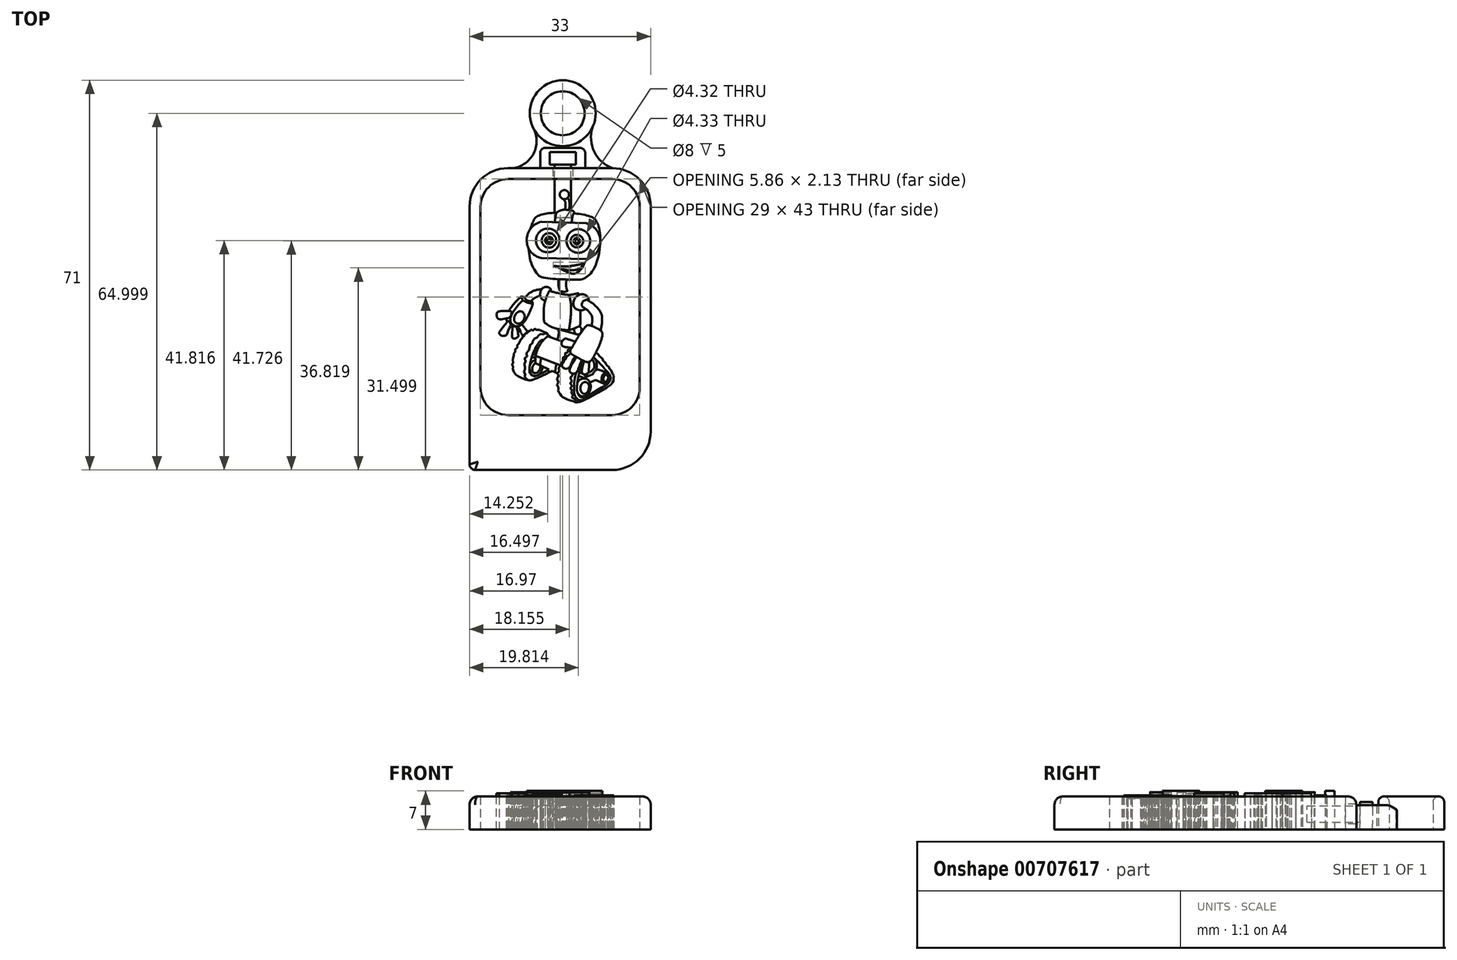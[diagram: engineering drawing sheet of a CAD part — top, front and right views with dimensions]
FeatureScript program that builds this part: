
annotation { "Feature Type Name" : "Feature", "Feature Type Description" : "" }
export const myFeature = defineFeature(function(context is Context, id is Id, definition is map)
    precondition{}
    {
        {
            var Q0;
            Q0=qCreatedBy(makeId("Top.planeOp"),FACE);
            var sketch = newSketch(context, id + "F0", { "sketchPlane" : qUnion([Q0])});
            skCircle(sketch, "E0", {"center": v(0.3, 18.7) * mm, "radius": 0.83 * mm});
            skFitSpline(sketch, "E1", {"points": [v(0.12, 17.9) * mm, v(0.47, 17.38) * mm, v(0.44, 15.96) * mm], "startDerivative": vector(0.9, -1.14) * mm, "endDerivative": vector(-0.07, -2.7) * mm});
            skFitSpline(sketch, "E2", {"points": [v(0.91, 18.15) * mm, v(1.19, 17.54) * mm, v(1.2, 15.9) * mm], "startDerivative": vector(0.78, -1.27) * mm, "endDerivative": vector(-0.02, -2.88) * mm});
            skCircle(sketch, "E3", {"center": v(-2.5, 10.36) * mm, "radius": 0.33 * mm});
            skCircle(sketch, "E4", {"center": v(-2.5, 10.36) * mm, "radius": 0.69 * mm});
            skCircle(sketch, "E5", {"center": v(-2.5, 10.36) * mm, "radius": 1.31 * mm});
            skCircle(sketch, "E6", {"center": v(2.58, 10.23) * mm, "radius": 0.33 * mm});
            skCircle(sketch, "E7", {"center": v(2.58, 10.23) * mm, "radius": 0.59 * mm});
            skCircle(sketch, "E8", {"center": v(2.58, 10.23) * mm, "radius": 1.15 * mm});
            skCircle(sketch, "E9", {"center": v(2.84, 10.27) * mm, "radius": 2.16 * mm});
            skPoint(sketch, "E9.first.point", {"position": v(4.19, 8.57) * mm});
            skPoint(sketch, "E9.second.point", {"position": v(4.6, 11.53) * mm});
            skPoint(sketch, "E9.third.point", {"position": v(0.83, 11.06) * mm});
            skCircle(sketch, "E10", {"center": v(-2.72, 10.36) * mm, "radius": 2.16 * mm});
            skPoint(sketch, "E10.first.point", {"position": v(-4.8, 10.92) * mm});
            skPoint(sketch, "E10.second.point", {"position": v(-3.27, 8.27) * mm});
            skPoint(sketch, "E10.third.point", {"position": v(-0.74, 11.23) * mm});
            skArc(sketch, "E11", {"start": v(-3.9, 13.75) * mm, "mid": v(-6.58, 10.45) * mm, "end": v(-3.92, 7.14) * mm});
            skArc(sketch, "E12", {"start": v(4.26, 6.95) * mm, "mid": v(6.85, 10.2) * mm, "end": v(4.28, 13.48) * mm});
            skLineSegment(sketch, "E13", {"start": v(-3.9, 13.75) * mm, "end": v(4.28, 13.48) * mm});
            skLineSegment(sketch, "E14", {"start": v(4.26, 6.95) * mm, "end": v(-3.92, 7.14) * mm});
            skFitSpline(sketch, "E15", {"points": [v(-1.45, 13.67) * mm, v(-1.34, 14.52) * mm, v(-1.2, 15.22) * mm, v(-1.1, 15.44) * mm, v(-0.38, 15.83) * mm, v(0.25, 15.96) * mm, v(0.44, 15.96) * mm, v(1.6, 15.83) * mm, v(2.03, 15.62) * mm, v(2.14, 15.45) * mm, v(2.16, 15.35) * mm, v(2.13, 15.29) * mm, v(2.02, 15.27) * mm, v(1.88, 15.13) * mm, v(1.62, 13.57) * mm], "startDerivative": vector(0.63, 8.93) * mm, "endDerivative": vector(-1.73, -15.25) * mm});
            skFitSpline(sketch, "E16", {"points": [v(-5.9, 12.47) * mm, v(-5.25, 14.1) * mm, v(-4.61, 14.77) * mm, v(-2.92, 15.27) * mm, v(-1.14, 15.4) * mm], "startDerivative": vector(2.4, 6.84) * mm, "endDerivative": vector(6.47, 0.13) * mm});
            skFitSpline(sketch, "E17", {"points": [v(-6.22, 8.92) * mm, v(-5.75, 6.26) * mm, v(-4.69, 4.3) * mm, v(-4.2, 3.84) * mm, v(-2.5, 3.43) * mm, v(0.92, 3.23) * mm, v(3.35, 3.25) * mm, v(4.25, 3.62) * mm, v(5.1, 4.38) * mm, v(6.1, 6.12) * mm, v(6.84, 10.02) * mm, v(6.6, 12.73) * mm, v(6.13, 13.9) * mm, v(5.7, 14.4) * mm, v(5.07, 14.7) * mm, v(3.8, 15.05) * mm, v(2.13, 15.29) * mm], "startDerivative": vector(2.92, -34.4) * mm, "endDerivative": vector(-27.68, 3.02) * mm});
            skFitSpline(sketch, "E18", {"points": [v(-1.75, 5.73) * mm, v(0.46, 5.61) * mm, v(2.53, 5.87) * mm, v(3.44, 6.09) * mm, v(4.12, 6.42) * mm], "startDerivative": vector(6.97, -0.72) * mm, "endDerivative": vector(3.62, 2.06) * mm});
            skFitSpline(sketch, "E19", {"points": [v(-1.75, 5.73) * mm, v(-0.96, 5.5) * mm, v(-0.2, 5.08) * mm, v(0.9, 4.56) * mm, v(1.74, 4.3) * mm, v(2.27, 4.34) * mm, v(3.1, 4.89) * mm, v(3.8, 5.89) * mm, v(3.9, 6.18) * mm, v(4.12, 6.42) * mm], "startDerivative": vector(7, -1.48) * mm, "endDerivative": vector(3.55, 3.32) * mm});
            skFitSpline(sketch, "E20", {"points": [v(-0.14, 5.6) * mm, v(-0.03, 5.1) * mm], "startDerivative": vector(0.1, -0.52) * mm, "endDerivative": vector(0.1, -0.52) * mm});
            skFitSpline(sketch, "E21", {"points": [v(-0.03, 5.1) * mm, v(0.8, 4.95) * mm, v(1.93, 4.94) * mm, v(2.96, 5.2) * mm, v(3.46, 5.49) * mm], "startDerivative": vector(3.26, -0.68) * mm, "endDerivative": vector(2.23, 1.53) * mm});
            skFitSpline(sketch, "E22", {"points": [v(3.46, 5.49) * mm, v(3.57, 6.14) * mm], "startDerivative": vector(0.1, 0.65) * mm, "endDerivative": vector(0.1, 0.65) * mm});
            skFitSpline(sketch, "E23", {"points": [v(-0.7, 1.73) * mm, v(-1, 1.68) * mm, v(-1.52, 1.57) * mm, v(-2.17, 1.34) * mm, v(-2.34, 1.21) * mm, v(-1.9, 1.02) * mm, v(-0.46, 0.67) * mm, v(0.7, 0.47) * mm, v(1.12, 0.44) * mm, v(1.38, 0.45) * mm, v(1.8, 0.52) * mm, v(2.6, 0.69) * mm, v(2.77, 0.77) * mm, v(2.73, 0.86) * mm, v(2.54, 1.01) * mm, v(1.61, 1.37) * mm, v(0.7, 1.58) * mm], "startDerivative": vector(-6.76, -0.7) * mm, "endDerivative": vector(-10.1, 1.55) * mm});
            skFitSpline(sketch, "E24", {"points": [v(-0.76, 3.3) * mm, v(-0.8, 2.67) * mm, v(-0.75, 1.97) * mm, v(-0.57, 1.3) * mm, v(-0.45, 1.13) * mm], "startDerivative": vector(-0.24, -2.28) * mm, "endDerivative": vector(0.93, -0.81) * mm});
            skFitSpline(sketch, "E25", {"points": [v(0.74, 3.24) * mm, v(0.64, 2.9) * mm, v(0.6, 2.27) * mm, v(0.66, 1.73) * mm, v(0.81, 1.31) * mm, v(0.85, 1.18) * mm], "startDerivative": vector(-0.63, -1.61) * mm, "endDerivative": vector(-0.1, -1.03) * mm});
            skFitSpline(sketch, "E26", {"points": [v(-0.45, 1.13) * mm, v(-0.22, 1.06) * mm, v(0.33, 1.01) * mm, v(0.7, 1.09) * mm, v(0.85, 1.18) * mm], "startDerivative": vector(0.96, -0.5) * mm, "endDerivative": vector(0.36, 0.85) * mm});
            skFitSpline(sketch, "E27", {"points": [v(1.12, 0.44) * mm, v(1.24, 0.2) * mm, v(1.38, -0.41) * mm, v(1.53, -1.74) * mm, v(1.38, -4.22) * mm, v(1.12, -5.92) * mm, v(1.04, -6) * mm, v(0.22, -5.93) * mm, v(-1.19, -5.72) * mm, v(-2.27, -5.29) * mm, v(-3.16, -4.72) * mm, v(-3.32, -4.57) * mm, v(-3.39, -4.44) * mm, v(-3.47, -3.34) * mm, v(-3.46, -2.3) * mm, v(-3.3, -1.07) * mm, v(-2.8, 0.44) * mm, v(-2.44, 1.14) * mm, v(-2.33, 1.25) * mm], "startDerivative": vector(7.24, -3.6) * mm, "endDerivative": vector(4.32, 3.3) * mm});
            skFitSpline(sketch, "E28", {"points": [v(1.04, -6) * mm, v(1.39, -5.9) * mm, v(2.36, -5.56) * mm, v(2.9, -5.32) * mm, v(3.1, -5.2) * mm, v(3.18, -5) * mm, v(3.21, -4.58) * mm, v(3.19, -2.37) * mm], "startDerivative": vector(2.66, 0.6) * mm, "endDerivative": vector(-0.15, 9.68) * mm});
            skFitSpline(sketch, "E29", {"points": [v(2.77, 0.79) * mm, v(2.82, 0.7) * mm, v(2.87, 0.37) * mm], "startDerivative": vector(0.07, -0.11) * mm, "endDerivative": vector(0.06, -0.59) * mm});
            skFitSpline(sketch, "E30", {"points": [v(-3.17, -0.58) * mm, v(-3.39, -0.55) * mm, v(-3.82, -0.28) * mm, v(-4.1, 0.29) * mm, v(-4.04, 1.06) * mm, v(-3.73, 1.58) * mm, v(-3.27, 1.86) * mm, v(-2.76, 1.88) * mm, v(-2.36, 1.68) * mm, v(-2.22, 1.54) * mm, v(-2.11, 1.36) * mm], "startDerivative": vector(-2.86, 0.03) * mm, "endDerivative": vector(1.55, -2.75) * mm});
            skFitSpline(sketch, "E31", {"points": [v(4.2, -2.1) * mm, v(3.83, -2.28) * mm, v(3.38, -2.4) * mm, v(3.19, -2.37) * mm, v(2.56, -2.2) * mm, v(2.14, -1.83) * mm, v(1.93, -1.09) * mm, v(2.2, -0.2) * mm, v(2.56, 0.19) * mm, v(2.87, 0.37) * mm, v(3.37, 0.54) * mm, v(4, 0.47) * mm, v(4.49, 0.12) * mm, v(4.73, -0.35) * mm, v(4.76, -0.66) * mm], "startDerivative": vector(-4.5, -3.3) * mm, "endDerivative": vector(0.01, -5.32) * mm});
            skFitSpline(sketch, "E32", {"points": [v(-3.48, -3.22) * mm, v(-1.78, -4.06) * mm, v(1.36, -4.43) * mm, v(3.2, -3.79) * mm], "startDerivative": vector(4.9, -3.02) * mm, "endDerivative": vector(5.37, 2.7) * mm});
            skFitSpline(sketch, "E33", {"points": [v(-3.84, 1.46) * mm, v(-4.94, 1.3) * mm, v(-6.15, 0.68) * mm, v(-6.87, -0.09) * mm], "startDerivative": vector(-3.3, -0.27) * mm, "endDerivative": vector(-2.02, -2.53) * mm});
            skFitSpline(sketch, "E34", {"points": [v(-4.08, 0.2) * mm, v(-4.4, 0.17) * mm, v(-5.23, -0.2) * mm, v(-5.69, -0.66) * mm], "startDerivative": vector(-1.12, 0.03) * mm, "endDerivative": vector(-1.09, -1.4) * mm});
            skFitSpline(sketch, "E35", {"points": [v(-6.87, -0.09) * mm, v(-6.78, -0.35) * mm, v(-6.22, -0.66) * mm, v(-5.8, -0.72) * mm, v(-5.69, -0.66) * mm], "startDerivative": vector(0.17, -1.2) * mm, "endDerivative": vector(0.62, 0.48) * mm});
            skFitSpline(sketch, "E36", {"points": [v(-5.65, -0.61) * mm, v(-5.52, -0.96) * mm, v(-5.55, -1.08) * mm, v(-5.79, -1.1) * mm, v(-6.43, -0.95) * mm, v(-7.26, -0.55) * mm, v(-7.32, -0.47) * mm, v(-7.53, 0.04) * mm, v(-7.46, 0.1) * mm, v(-6.84, -0.04) * mm], "startDerivative": vector(1.46, -3.36) * mm, "endDerivative": vector(5.12, -1.6) * mm});
            skFitSpline(sketch, "E37", {"points": [v(-7.4, 0.1) * mm, v(-7.53, 0.13) * mm, v(-7.7, 0.04) * mm, v(-8.25, -0.5) * mm, v(-9.37, -1.76) * mm, v(-9.7, -2.26) * mm, v(-9.85, -2.52) * mm], "startDerivative": vector(-1.54, 0.55) * mm, "endDerivative": vector(-1.06, -1.93) * mm});
            skFitSpline(sketch, "E38", {"points": [v(-5.54, -0.9) * mm, v(-5.48, -1.03) * mm, v(-5.48, -1.23) * mm, v(-6.29, -3.27) * mm, v(-6.98, -4.42) * mm, v(-7.46, -4.94) * mm, v(-8, -5.24) * mm, v(-8.74, -5.2) * mm, v(-9.4, -4.73) * mm, v(-9.52, -3.77) * mm, v(-9.1, -2.76) * mm, v(-8.38, -1.75) * mm, v(-7.3, -0.5) * mm], "startDerivative": vector(2.07, -4.05) * mm, "endDerivative": vector(10.06, 11.15) * mm});
            skEllipse(sketch, "E39", {"center": v(-7.91, -3.7) * mm, "majorRadius": 1.17 * mm, "minorRadius": 0.9 * mm, "majorAxis": v(0.45, 0.9)});
            skFitSpline(sketch, "E40", {"points": [v(-9.85, -3.75) * mm, v(-11.14, -4) * mm, v(-11.6, -4) * mm, v(-11.94, -3.67) * mm, v(-12.06, -3) * mm, v(-11.93, -2.73) * mm, v(-11.68, -2.58) * mm, v(-11.07, -2.52) * mm, v(-9.85, -2.52) * mm], "startDerivative": vector(-8, -1.73) * mm, "endDerivative": vector(7.43, -0.04) * mm});
            skFitSpline(sketch, "E41", {"points": [v(-9.85, -3.75) * mm, v(-9.6, -3.57) * mm, v(-9.39, -3.2) * mm, v(-9.34, -2.7) * mm, v(-9.52, -2.52) * mm, v(-9.85, -2.52) * mm], "startDerivative": vector(1.43, 0.8) * mm, "endDerivative": vector(-1.85, -0.22) * mm});
            skFitSpline(sketch, "E42", {"points": [v(4.38, -0.46) * mm, v(4.76, -0.66) * mm, v(5.4, -1.08) * mm, v(6.04, -1.64) * mm, v(6.54, -2.18) * mm, v(7.06, -3.11) * mm, v(7.16, -4.62) * mm, v(6.9, -6.06) * mm], "startDerivative": vector(3.69, -1.9) * mm, "endDerivative": vector(-2.34, -7.83) * mm});
            skFitSpline(sketch, "E43", {"points": [v(3.66, -1.78) * mm, v(4.2, -2.1) * mm, v(4.87, -2.73) * mm, v(5.32, -3.49) * mm, v(5.34, -4.62) * mm, v(5.24, -5.2) * mm], "startDerivative": vector(2.71, -1.62) * mm, "endDerivative": vector(-1.18, -2.93) * mm});
            skFitSpline(sketch, "E44", {"points": [v(6.9, -6.06) * mm, v(7.16, -6.34) * mm, v(7.23, -6.83) * mm, v(6.74, -8.54) * mm, v(5.58, -10.93) * mm, v(5.1, -11.56) * mm, v(4.63, -11.8) * mm, v(3.71, -11.54) * mm, v(1.8, -10.47) * mm, v(1.45, -10.2) * mm, v(1.37, -9.71) * mm, v(1.59, -9.3) * mm, v(2.54, -7.66) * mm, v(3.61, -6.06) * mm, v(4.2, -5.3) * mm, v(4.43, -5.1) * mm, v(5.24, -5.2) * mm, v(6.9, -6.06) * mm]});
            skFitSpline(sketch, "E45", {"points": [v(2.3, -8.07) * mm, v(0.6, -7.54) * mm, v(0.42, -7.54) * mm, v(0, -7.87) * mm, v(-0.23, -8.54) * mm, v(-0.05, -8.88) * mm, v(0.5, -9.08) * mm, v(1.68, -9.17) * mm], "startDerivative": vector(-9.45, 3.1) * mm, "endDerivative": vector(6.78, -0.26) * mm});
            skFitSpline(sketch, "E46", {"points": [v(3.87, -11.61) * mm, v(3.62, -12.64) * mm, v(3.48, -13.45) * mm, v(3.59, -13.84) * mm, v(3.9, -14.03) * mm, v(4.39, -13.95) * mm, v(4.76, -13.6) * mm, v(4.76, -13.41) * mm, v(4.85, -11.74) * mm], "startDerivative": vector(-1.62, -6.5) * mm, "endDerivative": vector(0.7, 10.55) * mm});
            skFitSpline(sketch, "E47", {"points": [v(3.5, -11.43) * mm, v(2.64, -13.52) * mm, v(2.48, -13.76) * mm, v(1.9, -13.9) * mm, v(1.36, -13.66) * mm, v(1.26, -13.3) * mm, v(1.44, -12.67) * mm, v(2.53, -10.9) * mm], "startDerivative": vector(-4.72, -11.44) * mm, "endDerivative": vector(5.93, 9.05) * mm});
            skFitSpline(sketch, "E48", {"points": [v(2.27, -10.74) * mm, v(1.68, -11.81) * mm, v(1.26, -12.74) * mm, v(0.92, -12.97) * mm, v(0.34, -12.97) * mm, v(-0.14, -12.43) * mm, v(0.2, -11.65) * mm, v(0.86, -10.73) * mm, v(1.45, -10.2) * mm], "startDerivative": vector(-3.77, -6.76) * mm, "endDerivative": vector(4.2, 4.03) * mm});
            skFitSpline(sketch, "E49", {"points": [v(3.66, -1.78) * mm, v(3.48, -1.45) * mm, v(3.71, -0.73) * mm, v(4.38, -0.46) * mm], "startDerivative": vector(-0.94, 1.03) * mm, "endDerivative": vector(1.87, 0.43) * mm});
            skFitSpline(sketch, "E50", {"points": [v(1.6, -9.27) * mm, v(1.43, -9.26) * mm, v(1.38, -9.44) * mm, v(0.97, -9.54) * mm, v(0.86, -10.03) * mm, v(0.46, -10.2) * mm, v(0.48, -10.7) * mm, v(0.05, -10.97) * mm, v(0.07, -11.56) * mm, v(-0.23, -11.9) * mm, v(-0.38, -12.43) * mm, v(-0.7, -12.82) * mm, v(-0.7, -13.5) * mm, v(-0.98, -13.83) * mm, v(-0.79, -14.3) * mm, v(-1.05, -14.84) * mm, v(-0.8, -15.5) * mm, v(-1.05, -15.84) * mm, v(-0.76, -16.5) * mm, v(-0.84, -16.9) * mm, v(-0.46, -17.65) * mm, v(0.2, -18.28) * mm, v(2.04, -19.01) * mm, v(3.13, -19.05) * mm, v(8.56, -16.08) * mm, v(9.01, -15.65) * mm, v(9.15, -15.34) * mm, v(9.27, -15.14) * mm, v(9.21, -14.97) * mm, v(9.34, -14.75) * mm, v(9.22, -14.49) * mm, v(9.3, -14.28) * mm, v(9.09, -13.91) * mm, v(9.1, -13.77) * mm, v(8.78, -13.4) * mm, v(8.8, -13.21) * mm, v(8.42, -12.89) * mm, v(8.5, -12.75) * mm, v(8.04, -12.43) * mm, v(8.07, -12.32) * mm, v(7.7, -11.97) * mm, v(7.73, -11.8) * mm, v(7.36, -11.56) * mm, v(7.37, -11.31) * mm, v(7, -11.1) * mm, v(7.02, -10.98) * mm, v(6.72, -10.73) * mm, v(6.7, -10.61) * mm, v(6.38, -10.44) * mm, v(6.38, -10.26) * mm, v(6.04, -10.08) * mm], "startDerivative": vector(-15.2, 2.24) * mm, "endDerivative": vector(-28.52, 9.44) * mm});
            skFitSpline(sketch, "E51", {"points": [v(1.67, -13.87) * mm, v(1.76, -14.28) * mm, v(1.38, -14.65) * mm, v(1.68, -15.3) * mm, v(1.38, -15.62) * mm, v(1.68, -16.15) * mm, v(1.38, -16.5) * mm, v(1.68, -16.92) * mm, v(1.59, -17.5) * mm, v(1.87, -17.85) * mm, v(1.68, -18.2) * mm, v(2.3, -18.66) * mm, v(2.48, -18.94) * mm, v(3.13, -19.05) * mm], "startDerivative": vector(3.43, -6.3) * mm, "endDerivative": vector(10.14, -0.04) * mm});
            skFitSpline(sketch, "E52", {"points": [v(2.48, -13.76) * mm, v(2.24, -14.48) * mm, v(2.06, -16.55) * mm, v(2.2, -17.86) * mm, v(2.9, -18.7) * mm, v(3.92, -18.64) * mm, v(4.67, -18.36) * mm], "startDerivative": vector(-1.23, -4.5) * mm, "endDerivative": vector(4.87, 2.34) * mm});
            skFitSpline(sketch, "E53", {"points": [v(3.71, -11.54) * mm, v(3.17, -13.15) * mm, v(2.74, -15.07) * mm, v(2.68, -17.36) * mm, v(3.27, -18.17) * mm, v(4.2, -18.1) * mm, v(7.11, -16.42) * mm, v(8.4, -15.53) * mm, v(8.72, -14.56) * mm, v(8.07, -13.52) * mm, v(6.64, -11.91) * mm, v(5.58, -10.93) * mm], "startDerivative": vector(-6.92, -17.06) * mm, "endDerivative": vector(-12.58, 10.17) * mm});
            skFitSpline(sketch, "E54", {"points": [v(2.65, -15.66) * mm, v(3.13, -15.01) * mm, v(4.2, -14.82) * mm, v(4.87, -15.37) * mm, v(5.1, -16.33) * mm, v(4.73, -17.48) * mm, v(4.2, -17.94) * mm, v(3.71, -18.07) * mm, v(3.13, -17.92) * mm, v(2.68, -17.36) * mm], "startDerivative": vector(3.07, 6.78) * mm, "endDerivative": vector(-2.95, 6.13) * mm});
            skLineSegment(sketch, "E55", {"start": v(4.2, -14.82) * mm, "end": v(2.88, -14.32) * mm});
            skLineSegment(sketch, "E56", {"start": v(4.95, -15.52) * mm, "end": v(5.98, -15.08) * mm});
            skLineSegment(sketch, "E57", {"start": v(5.98, -15.08) * mm, "end": v(7.58, -15.75) * mm});
            skEllipse(sketch, "E58", {"center": v(4.01, -16.5) * mm, "majorRadius": 1.09 * mm, "minorRadius": 0.78 * mm, "majorAxis": v(0.16, 0.99)});
            skEllipse(sketch, "E59", {"center": v(7.83, -14.75) * mm, "majorRadius": 0.63 * mm, "minorRadius": 0.45 * mm, "majorAxis": v(0.27, 0.96)});
            skEllipse(sketch, "E60", {"center": v(7.83, -14.75) * mm, "majorRadius": 1.03 * mm, "minorRadius": 0.75 * mm, "majorAxis": v(-0.24, -0.97)});
            skFitSpline(sketch, "E61", {"points": [v(5.98, -15.08) * mm, v(5.62, -14.73) * mm, v(5.5, -14.2) * mm, v(5.65, -13.69) * mm, v(5.98, -13.32) * mm, v(6.33, -13.16) * mm, v(6.48, -13.17) * mm], "startDerivative": vector(-2.22, 1.68) * mm, "endDerivative": vector(1.4, -0.29) * mm});
            skLineSegment(sketch, "E62", {"start": v(6.48, -13.17) * mm, "end": v(8.14, -13.77) * mm});
            skLineSegment(sketch, "E63", {"start": v(3.79, -14.66) * mm, "end": v(5.52, -14) * mm});
            skFitSpline(sketch, "E64", {"points": [v(3.04, -13.64) * mm, v(4.2, -14.23) * mm, v(4.52, -14.3) * mm, v(4.9, -14.24) * mm], "startDerivative": vector(2.74, -1.49) * mm, "endDerivative": vector(1.52, 0.33) * mm});
            skFitSpline(sketch, "E65", {"points": [v(5.8, -11.1) * mm, v(6.2, -11.92) * mm, v(6.11, -13.04) * mm, v(5.98, -13.32) * mm], "startDerivative": vector(1.4, -1.95) * mm, "endDerivative": vector(-0.64, -1) * mm});
            skFitSpline(sketch, "E66", {"points": [v(3.43, -12.3) * mm, v(3.4, -12.94) * mm, v(3.48, -13.45) * mm], "startDerivative": vector(-0.12, -1.25) * mm, "endDerivative": vector(0.22, -1.05) * mm});
            skFitSpline(sketch, "E67", {"points": [v(5.26, -11.4) * mm, v(5.57, -11.6) * mm, v(5.77, -12.6) * mm, v(5.38, -13.32) * mm, v(4.94, -13.63) * mm, v(4.73, -13.65) * mm], "startDerivative": vector(1.96, -0.71) * mm, "endDerivative": vector(-1.59, 0.06) * mm});
            skLineSegment(sketch, "E68", {"start": v(-2.77, -7.1) * mm, "end": v(-0.11, -8.05) * mm});
            skFitSpline(sketch, "E69", {"points": [v(-2.77, -7.1) * mm, v(-3.76, -8.1) * mm, v(-4.58, -9.48) * mm, v(-4.98, -11) * mm, v(-4.98, -12.02) * mm], "startDerivative": vector(-4.13, -3.72) * mm, "endDerivative": vector(0.28, -4.5) * mm});
            skLineSegment(sketch, "E70", {"start": v(-4.98, -12.02) * mm, "end": v(-0.98, -13.83) * mm});
            skLineSegment(sketch, "E71", {"start": v(-4.94, -10.69) * mm, "end": v(-0.38, -12.43) * mm});
            skFitSpline(sketch, "E72", {"points": [v(-3.9, -11.08) * mm, v(-4.04, -11.64) * mm, v(-4.07, -12.43) * mm], "startDerivative": vector(-0.58, -1.59) * mm, "endDerivative": vector(0.13, -1.26) * mm});
            skFitSpline(sketch, "E73", {"points": [v(-1.11, -12.15) * mm, v(-1.3, -12.88) * mm, v(-1.33, -13.68) * mm], "startDerivative": vector(-0.59, -1.61) * mm, "endDerivative": vector(0.18, -1.44) * mm});
            skFitSpline(sketch, "E74", {"points": [v(-10.25, -3.83) * mm, v(-10.23, -4.14) * mm, v(-10.1, -4.43) * mm], "startDerivative": vector(0, -0.64) * mm, "endDerivative": vector(0.32, -0.56) * mm});
            skFitSpline(sketch, "E75", {"points": [v(-10.1, -4.43) * mm, v(-11.55, -6.34) * mm, v(-11.6, -6.47) * mm, v(-11.5, -6.69) * mm, v(-11.18, -6.98) * mm, v(-10.8, -7.04) * mm, v(-10.32, -6.92) * mm, v(-10.21, -6.75) * mm, v(-9.48, -5.02) * mm, v(-9.5, -4.87) * mm, v(-9.71, -4.49) * mm, v(-9.84, -4.37) * mm, v(-10.04, -4.37) * mm, v(-10.1, -4.43) * mm]});
            skFitSpline(sketch, "E76", {"points": [v(-9.48, -5.02) * mm, v(-9, -5.24) * mm, v(-8.42, -5.34) * mm, v(-8, -5.24) * mm], "startDerivative": vector(1.34, -0.74) * mm, "endDerivative": vector(1.3, 0.44) * mm});
            skFitSpline(sketch, "E77", {"points": [v(-9.15, -5.18) * mm, v(-9.24, -7.14) * mm, v(-9.2, -7.4) * mm, v(-8.88, -7.52) * mm, v(-8.59, -7.46) * mm, v(-8.19, -7.2) * mm, v(-8.09, -6.96) * mm, v(-8.42, -5.34) * mm], "startDerivative": vector(-0.42, -9.45) * mm, "endDerivative": vector(-2.16, 8.56) * mm});
            skFitSpline(sketch, "E78", {"points": [v(-2.33, -7.25) * mm, v(-2.32, -7.1) * mm, v(-2.67, -6.94) * mm, v(-2.67, -6.77) * mm, v(-4.55, -5.92) * mm, v(-4.84, -5.92) * mm, v(-5.1, -5.76) * mm, v(-5.47, -6.03) * mm, v(-5.8, -5.9) * mm, v(-6.01, -6.18) * mm, v(-6.3, -6.17) * mm, v(-6.48, -6.55) * mm, v(-6.88, -6.62) * mm, v(-7, -7.05) * mm, v(-7.35, -7.14) * mm, v(-7.42, -7.6) * mm, v(-7.8, -7.83) * mm, v(-7.86, -8.37) * mm, v(-8.27, -8.66) * mm, v(-8.27, -9.1) * mm, v(-8.65, -9.47) * mm, v(-8.68, -10.02) * mm, v(-8.97, -10.35) * mm, v(-8.87, -10.76) * mm, v(-9.15, -11.23) * mm, v(-9, -11.77) * mm, v(-9.21, -12.18) * mm, v(-9.02, -12.66) * mm, v(-9.1, -13.05) * mm, v(-8.66, -14) * mm, v(-8.24, -14.36) * mm, v(-6.87, -14.98) * mm, v(-5.82, -15.11) * mm, v(-1.92, -13.4) * mm], "startDerivative": vector(4.57, 10.26) * mm, "endDerivative": vector(54.83, 27.76) * mm});
            skFitSpline(sketch, "E79", {"points": [v(-8.12, -5.28) * mm, v(-7.37, -6.88) * mm, v(-7.23, -6.96) * mm, v(-6.96, -6.94) * mm], "startDerivative": vector(1.52, -3.53) * mm, "endDerivative": vector(1.33, 0.21) * mm});
            skFitSpline(sketch, "E80", {"points": [v(-7.46, -4.94) * mm, v(-7.05, -5.44) * mm, v(-6.6, -6.02) * mm, v(-6.53, -6.13) * mm, v(-6.52, -6.4) * mm, v(-6.6, -6.58) * mm], "startDerivative": vector(1.44, -1.7) * mm, "endDerivative": vector(-0.68, -1.04) * mm});
            skFitSpline(sketch, "E81", {"points": [v(-2.67, -6.77) * mm, v(-3.04, -6.63) * mm, v(-3.34, -6.55) * mm, v(-3.72, -6.77) * mm, v(-4, -6.66) * mm, v(-4.22, -6.96) * mm, v(-4.5, -6.96) * mm, v(-4.66, -7.33) * mm, v(-5.04, -7.4) * mm, v(-5.13, -7.8) * mm, v(-5.49, -7.92) * mm, v(-5.56, -8.4) * mm, v(-5.9, -8.54) * mm, v(-5.94, -9.12) * mm, v(-6.26, -9.37) * mm, v(-6.2, -9.85) * mm, v(-6.7, -10.26) * mm, v(-6.48, -10.86) * mm, v(-6.93, -11.14) * mm, v(-6.74, -11.68) * mm, v(-7.05, -12.02) * mm, v(-6.75, -12.47) * mm, v(-7.07, -12.82) * mm, v(-6.84, -13.2) * mm, v(-7.05, -13.67) * mm, v(-6.78, -14.01) * mm, v(-7.06, -14.29) * mm, v(-6.65, -14.67) * mm, v(-6.61, -14.96) * mm, v(-6.17, -15.15) * mm], "startDerivative": vector(-11.53, 3.84) * mm, "endDerivative": vector(16.6, -3.55) * mm});
            skFitSpline(sketch, "E82", {"points": [v(-2.48, -13.16) * mm, v(-4.42, -14.13) * mm, v(-5.25, -14.35) * mm, v(-5.96, -13.83) * mm, v(-5.98, -12.31) * mm, v(-5.38, -10.14) * mm, v(-4.22, -8.1) * mm, v(-3.76, -7.79) * mm, v(-3.5, -7.79) * mm], "startDerivative": vector(-12.89, -6.58) * mm, "endDerivative": vector(4.5, -0.52) * mm});
            skFitSpline(sketch, "E83", {"points": [v(-3.72, -12.6) * mm, v(-3.72, -12.97) * mm, v(-3.98, -13.62) * mm, v(-4.65, -14.24) * mm, v(-5.24, -14.3) * mm, v(-5.74, -14.02) * mm, v(-5.97, -13.44) * mm, v(-6.03, -12.64) * mm, v(-5.67, -11.88) * mm, v(-5.2, -11.5) * mm, v(-5, -11.43) * mm], "startDerivative": vector(0.38, -4.4) * mm, "endDerivative": vector(2.97, 0.62) * mm});
            skFitSpline(sketch, "E84", {"points": [v(-5.65, -10.9) * mm, v(-5.2, -11) * mm, v(-5, -11.19) * mm], "startDerivative": vector(0.57, -0.15) * mm, "endDerivative": vector(0.38, -0.44) * mm});
            skFitSpline(sketch, "E85", {"points": [v(-5.43, -10.26) * mm, v(-4.91, -10.55) * mm], "startDerivative": vector(0.52, -0.28) * mm, "endDerivative": vector(0.52, -0.28) * mm});
            skFitSpline(sketch, "E86", {"points": [v(-4.73, -8.82) * mm, v(-4.98, -9.84) * mm, v(-4.87, -10.35) * mm], "startDerivative": vector(-1.14, -2.41) * mm, "endDerivative": vector(0.44, -1.13) * mm});
            skFitSpline(sketch, "E87", {"points": [v(-0.82, -5.8) * mm, v(-0.85, -5.94) * mm, v(-0.7, -6.17) * mm, v(-0.77, -6.3) * mm, v(-0.68, -6.54) * mm, v(-0.77, -6.63) * mm, v(-0.67, -6.8) * mm, v(-0.8, -6.87) * mm, v(-0.7, -7.08) * mm, v(-0.84, -7.18) * mm, v(-0.81, -7.39) * mm, v(-0.97, -7.48) * mm, v(-1, -7.63) * mm, v(-1.2, -7.66) * mm], "startDerivative": vector(-1.06, -2.03) * mm, "endDerivative": vector(-3.33, 0.28) * mm});
            skFitSpline(sketch, "E88", {"points": [v(2.17, -5.64) * mm, v(2.1, -5.99) * mm, v(2.29, -6.55) * mm, v(2.76, -6.78) * mm, v(3.22, -6.6) * mm], "startDerivative": vector(-0.53, -1.47) * mm, "endDerivative": vector(1.55, 1.3) * mm});
            skFitSpline(sketch, "E89", {"points": [v(2.98, -5.29) * mm, v(3.3, -5.53) * mm, v(3.42, -5.95) * mm, v(3.3, -6.49) * mm], "startDerivative": vector(1.17, -0.65) * mm, "endDerivative": vector(-0.68, -1.55) * mm});
            skLineSegment(sketch, "E90", {"start": v(-0.82, -5.8) * mm, "end": v(2.58, -6.75) * mm});
            skFitSpline(sketch, "E91", {"points": [v(-4.99, -11.96) * mm, v(-5.32, -12.33) * mm, v(-5.56, -13.07) * mm, v(-5.48, -13.55) * mm, v(-5.21, -13.8) * mm, v(-4.76, -13.77) * mm, v(-4.3, -13.35) * mm, v(-4.1, -12.9) * mm, v(-4.1, -12.57) * mm, v(-4.12, -12.4) * mm], "startDerivative": vector(-3.02, -2.7) * mm, "endDerivative": vector(-0.42, 2.2) * mm});
            skSolve(sketch);
        }
        {
            var Q0;
            {var subQ1=sQuery(id+"F0.wireOp",EDGE,"E44");var subQ12=makeQuery(id+"F0.imprint","INTERSECT",VERTEX,{"derivedFrom":[sQuery(id+"F0.wireOp",EDGE,"E42"),subQ1]});Q0=makeQuery(id+"F0.imprint","IMPRINT",FACE,{"disambiguationData":[TD([[makeQuery(id+"F0.imprint","IMPRINT",EDGE,{"disambiguationData":[TD([[subQ12,-1.0]])],"derivedFrom":subQ1}),-1.0]])]});}
            var Q1;
            Q1=makeQuery(id+"F0.imprint","IMPRINT",FACE,{"disambiguationData":[TD([[makeQuery(id+"F0.imprint","IMPRINT",EDGE,{"derivedFrom":sQuery(id+"F0.wireOp",EDGE,"E9")}),-1.0]])]});
            var Q2;
            {var subQ0=sQuery(id+"F0.wireOp",EDGE,"E0");var subQ1=makeQuery(id+"F0.imprint","INTERSECT",VERTEX,{"derivedFrom":[subQ0,sQuery(id+"F0.wireOp",EDGE,"E1")]});Q2=makeQuery(id+"F0.imprint","IMPRINT",FACE,{"disambiguationData":[TD([[makeQuery(id+"F0.imprint","IMPRINT",EDGE,{"disambiguationData":[TD([[subQ1,-1.0]])],"derivedFrom":subQ0}),1.0]])]});}
            extrude(context, id + "F1", {"entities" : qUnion([Q0, Q1, Q2]), "depth" : 7 * mm, "offsetDistance" : 25 * mm});
        }
        {
            var Q0;
            {var subQ0=sQuery(id+"F0.wireOp",EDGE,"E45");var subQ1=sQuery(id+"F0.wireOp",EDGE,"E44");var subQ2=makeQuery(id+"F0.imprint","INTERSECT",VERTEX,{"disambiguationData":[OD(0.0)],"derivedFrom":[subQ1,subQ0]});Q0=makeQuery(id+"F0.imprint","IMPRINT",FACE,{"disambiguationData":[TD([[makeQuery(id+"F0.imprint","IMPRINT",EDGE,{"disambiguationData":[TD([[subQ2,1.0]])],"derivedFrom":subQ1}),1.0]])]});}
            var Q1;
            {var subQ0=sQuery(id+"F0.wireOp",EDGE,"E48");Q1=makeQuery(id+"F0.imprint","IMPRINT",FACE,{"disambiguationData":[TD([[makeQuery(id+"F0.imprint","IMPRINT",EDGE,{"derivedFrom":subQ0}),-1.0]])]});}
            var Q2;
            {var subQ0=sQuery(id+"F0.wireOp",EDGE,"E47");var subQ1=sQuery(id+"F0.wireOp",EDGE,"E44");var subQ2=makeQuery(id+"F0.imprint","INTERSECT",VERTEX,{"disambiguationData":[OD(0.0)],"derivedFrom":[subQ1,subQ0]});Q2=makeQuery(id+"F0.imprint","IMPRINT",FACE,{"disambiguationData":[TD([[makeQuery(id+"F0.imprint","IMPRINT",EDGE,{"disambiguationData":[TD([[subQ2,-1.0]])],"derivedFrom":subQ1}),1.0]])]});}
            var Q3;
            {var subQ0=sQuery(id+"F0.wireOp",EDGE,"E46");var subQ1=sQuery(id+"F0.wireOp",EDGE,"E44");var subQ2=makeQuery(id+"F0.imprint","INTERSECT",VERTEX,{"disambiguationData":[OD(0.0)],"derivedFrom":[subQ1,subQ0]});Q3=makeQuery(id+"F0.imprint","IMPRINT",FACE,{"disambiguationData":[TD([[makeQuery(id+"F0.imprint","IMPRINT",EDGE,{"disambiguationData":[TD([[subQ2,1.0]])],"derivedFrom":subQ1}),1.0]])]});}
            var Q4;
            {var subQ3=sQuery(id+"F0.wireOp",EDGE,"E49");Q4=makeQuery(id+"F0.imprint","IMPRINT",FACE,{"disambiguationData":[TD([[makeQuery(id+"F0.imprint","IMPRINT",EDGE,{"derivedFrom":subQ3}),1.0]])]});}
            var Q5;
            {var subQ3=sQuery(id+"F0.wireOp",EDGE,"E27");var subQ5=sQuery(id+"F0.wireOp",EDGE,"E23");var subQ6=makeQuery(id+"F0.imprint","INTERSECT",VERTEX,{"disambiguationData":[OD(1.0)],"derivedFrom":[subQ5,subQ3]});Q5=makeQuery(id+"F0.imprint","IMPRINT",FACE,{"disambiguationData":[TD([[makeQuery(id+"F0.imprint","IMPRINT",EDGE,{"disambiguationData":[TD([[subQ6,1.0]])],"derivedFrom":subQ5}),-1.0]])]});}
            var Q6;
            Q6=makeQuery(id+"F0.imprint","IMPRINT",FACE,{"disambiguationData":[TD([[makeQuery(id+"F0.imprint","IMPRINT",EDGE,{"derivedFrom":sQuery(id+"F0.wireOp",EDGE,"E39")}),-1.0]])]});
            var Q7;
            Q7=makeQuery(id+"F0.imprint","IMPRINT",FACE,{"disambiguationData":[TD([[makeQuery(id+"F0.imprint","IMPRINT",EDGE,{"derivedFrom":sQuery(id+"F0.wireOp",EDGE,"E3")}),1.0]])]});
            var Q8;
            Q8=makeQuery(id+"F0.imprint","IMPRINT",FACE,{"disambiguationData":[TD([[makeQuery(id+"F0.imprint","IMPRINT",EDGE,{"derivedFrom":sQuery(id+"F0.wireOp",EDGE,"E6")}),1.0]])]});
            var Q9;
            {var subQ0=sQuery(id+"F0.wireOp",EDGE,"E15");var subQ3=sQuery(id+"F0.wireOp",EDGE,"E13");var subQ4=makeQuery(id+"F0.imprint","INTERSECT",VERTEX,{"disambiguationData":[OD(0.0)],"derivedFrom":[subQ3,subQ0]});Q9=makeQuery(id+"F0.imprint","IMPRINT",FACE,{"disambiguationData":[TD([[makeQuery(id+"F0.imprint","IMPRINT",EDGE,{"disambiguationData":[TD([[subQ4,-1.0]])],"derivedFrom":subQ3}),1.0]])]});}
            extrude(context, id + "F2", {"entities" : qUnion([Q0, Q1, Q2, Q3, Q4, Q5, Q6, Q7, Q8, Q9]), "depth" : 6.8 * mm, "offsetDistance" : 25 * mm});
        }
        {
            var Q0;
            {var subQ4=sQuery(id+"F0.wireOp",EDGE,"E14");Q0=makeQuery(id+"F0.imprint","IMPRINT",FACE,{"disambiguationData":[TD([[makeQuery(id+"F0.imprint","IMPRINT",EDGE,{"derivedFrom":subQ4}),1.0]])]});}
            var Q1;
            {var subQ3=sQuery(id+"F0.wireOp",EDGE,"E16");Q1=makeQuery(id+"F0.imprint","IMPRINT",FACE,{"disambiguationData":[TD([[makeQuery(id+"F0.imprint","IMPRINT",EDGE,{"derivedFrom":subQ3}),-1.0]])]});}
            var Q2;
            {var subQ0=sQuery(id+"F0.wireOp",EDGE,"E13");var subQ1=sQuery(id+"F0.wireOp",EDGE,"E12");var subQ2=makeQuery(id+"F0.imprint","INTERSECT",VERTEX,{"derivedFrom":[subQ1,subQ0]});Q2=makeQuery(id+"F0.imprint","IMPRINT",FACE,{"disambiguationData":[TD([[makeQuery(id+"F0.imprint","IMPRINT",EDGE,{"disambiguationData":[TD([[subQ2,1.0]])],"derivedFrom":subQ1}),-1.0]])]});}
            var Q3;
            {var subQ5=sQuery(id+"F0.wireOp",EDGE,"E49");Q3=makeQuery(id+"F0.imprint","IMPRINT",FACE,{"disambiguationData":[TD([[makeQuery(id+"F0.imprint","IMPRINT",EDGE,{"derivedFrom":subQ5}),-1.0]])]});}
            var Q4;
            {var subQ5=sQuery(id+"F0.wireOp",EDGE,"E35");Q4=makeQuery(id+"F0.imprint","IMPRINT",FACE,{"disambiguationData":[TD([[makeQuery(id+"F0.imprint","IMPRINT",EDGE,{"derivedFrom":subQ5}),1.0]])]});}
            var Q5;
            Q5=makeQuery(id+"F0.imprint","IMPRINT",FACE,{"disambiguationData":[TD([[makeQuery(id+"F0.imprint","IMPRINT",EDGE,{"derivedFrom":sQuery(id+"F0.wireOp",EDGE,"E39")}),1.0]])]});
            var Q6;
            {var subQ0=sQuery(id+"F0.wireOp",EDGE,"E79");Q6=makeQuery(id+"F0.imprint","IMPRINT",FACE,{"disambiguationData":[TD([[makeQuery(id+"F0.imprint","IMPRINT",EDGE,{"derivedFrom":subQ0}),1.0]])]});}
            var Q7;
            {var subQ0=sQuery(id+"F0.wireOp",EDGE,"E77");Q7=makeQuery(id+"F0.imprint","IMPRINT",FACE,{"disambiguationData":[TD([[makeQuery(id+"F0.imprint","IMPRINT",EDGE,{"derivedFrom":subQ0}),1.0]])]});}
            var Q8;
            {var subQ0=sQuery(id+"F0.wireOp",EDGE,"E75");var subQ1=makeQuery(id+"F0.imprint","INTERSECT",VERTEX,{"derivedFrom":[sQuery(id+"F0.wireOp",EDGE,"E74"),subQ0]});Q8=makeQuery(id+"F0.imprint","IMPRINT",FACE,{"disambiguationData":[TD([[makeQuery(id+"F0.imprint","IMPRINT",EDGE,{"disambiguationData":[TD([[subQ1,-1.0]])],"derivedFrom":subQ0}),1.0]])]});}
            var Q9;
            {var subQ0=sQuery(id+"F0.wireOp",EDGE,"E41");Q9=makeQuery(id+"F0.imprint","IMPRINT",FACE,{"disambiguationData":[TD([[makeQuery(id+"F0.imprint","IMPRINT",EDGE,{"derivedFrom":subQ0}),1.0]])]});}
            var Q10;
            {var subQ1=sQuery(id+"F0.wireOp",EDGE,"E27");var subQ4=sQuery(id+"F0.wireOp",EDGE,"E28");var subQ6=makeQuery(id+"F0.imprint","INTERSECT",VERTEX,{"disambiguationData":[OD(1.0)],"derivedFrom":[subQ1,subQ4]});Q10=makeQuery(id+"F0.imprint","IMPRINT",FACE,{"disambiguationData":[TD([[makeQuery(id+"F0.imprint","IMPRINT",EDGE,{"disambiguationData":[TD([[subQ6,1.0]])],"derivedFrom":subQ1}),-1.0]])]});}
            var Q11;
            {var subQ0=sQuery(id+"F0.wireOp",EDGE,"E27");var subQ4=sQuery(id+"F0.wireOp",EDGE,"E23");var subQ6=makeQuery(id+"F0.imprint","INTERSECT",VERTEX,{"disambiguationData":[OD(0.0)],"derivedFrom":[subQ4,subQ0]});Q11=makeQuery(id+"F0.imprint","IMPRINT",FACE,{"disambiguationData":[TD([[makeQuery(id+"F0.imprint","IMPRINT",EDGE,{"disambiguationData":[TD([[subQ6,1.0]])],"derivedFrom":subQ4}),-1.0]])]});}
            var Q12;
            {var subQ3=sQuery(id+"F0.wireOp",EDGE,"E72");Q12=makeQuery(id+"F0.imprint","IMPRINT",FACE,{"disambiguationData":[TD([[makeQuery(id+"F0.imprint","IMPRINT",EDGE,{"derivedFrom":subQ3}),-1.0]])]});}
            var Q13;
            {var subQ5=sQuery(id+"F0.wireOp",EDGE,"E73");Q13=makeQuery(id+"F0.imprint","IMPRINT",FACE,{"disambiguationData":[TD([[makeQuery(id+"F0.imprint","IMPRINT",EDGE,{"derivedFrom":subQ5}),1.0]])]});}
            var Q14;
            Q14=makeQuery(id+"F0.imprint","IMPRINT",FACE,{"disambiguationData":[TD([[makeQuery(id+"F0.imprint","IMPRINT",EDGE,{"derivedFrom":sQuery(id+"F0.wireOp",EDGE,"E6")}),-1.0]])]});
            var Q15;
            Q15=makeQuery(id+"F0.imprint","IMPRINT",FACE,{"disambiguationData":[TD([[makeQuery(id+"F0.imprint","IMPRINT",EDGE,{"derivedFrom":sQuery(id+"F0.wireOp",EDGE,"E3")}),-1.0]])]});
            extrude(context, id + "F3", {"entities" : qUnion([Q0, Q1, Q2, Q3, Q4, Q5, Q6, Q7, Q8, Q9, Q10, Q11, Q12, Q13, Q14, Q15]), "depth" : 6.6 * mm, "offsetDistance" : 25 * mm});
        }
        {
            var Q0;
            {var subQ9=sQuery(id+"F0.wireOp",EDGE,"E37");Q0=makeQuery(id+"F0.imprint","IMPRINT",FACE,{"disambiguationData":[TD([[makeQuery(id+"F0.imprint","IMPRINT",EDGE,{"derivedFrom":subQ9}),1.0]])]});}
            var Q1;
            {var subQ9=sQuery(id+"F0.wireOp",EDGE,"E29");Q1=makeQuery(id+"F0.imprint","IMPRINT",FACE,{"disambiguationData":[TD([[makeQuery(id+"F0.imprint","IMPRINT",EDGE,{"derivedFrom":subQ9}),-1.0]])]});}
            var Q2;
            {var subQ1=sQuery(id+"F0.wireOp",EDGE,"E28");var subQ5=sQuery(id+"F0.wireOp",EDGE,"E27");var subQ7=makeQuery(id+"F0.imprint","INTERSECT",VERTEX,{"disambiguationData":[OD(1.0)],"derivedFrom":[subQ5,subQ1]});Q2=makeQuery(id+"F0.imprint","IMPRINT",FACE,{"disambiguationData":[TD([[makeQuery(id+"F0.imprint","IMPRINT",EDGE,{"disambiguationData":[TD([[subQ7,1.0]])],"derivedFrom":subQ5}),1.0]])]});}
            var Q3;
            {var subQ5=sQuery(id+"F0.wireOp",EDGE,"E72");Q3=makeQuery(id+"F0.imprint","IMPRINT",FACE,{"disambiguationData":[TD([[makeQuery(id+"F0.imprint","IMPRINT",EDGE,{"derivedFrom":subQ5}),1.0]])]});}
            var Q4;
            {var subQ0=sQuery(id+"F0.wireOp",EDGE,"E1");Q4=makeQuery(id+"F0.imprint","IMPRINT",FACE,{"disambiguationData":[TD([[makeQuery(id+"F0.imprint","IMPRINT",EDGE,{"derivedFrom":subQ0}),1.0]])]});}
            var Q5;
            {var subQ3=sQuery(id+"F0.wireOp",EDGE,"E81");Q5=makeQuery(id+"F0.imprint","IMPRINT",FACE,{"disambiguationData":[TD([[makeQuery(id+"F0.imprint","IMPRINT",EDGE,{"derivedFrom":subQ3}),1.0]])]});}
            var Q6;
            {var subQ14=sQuery(id+"F0.wireOp",EDGE,"E52");Q6=makeQuery(id+"F0.imprint","IMPRINT",FACE,{"disambiguationData":[TD([[makeQuery(id+"F0.imprint","IMPRINT",EDGE,{"derivedFrom":subQ14}),1.0]])]});}
            var Q7;
            {var subQ0=sQuery(id+"F0.wireOp",EDGE,"E20");Q7=makeQuery(id+"F0.imprint","IMPRINT",FACE,{"disambiguationData":[TD([[makeQuery(id+"F0.imprint","IMPRINT",EDGE,{"derivedFrom":subQ0}),1.0]])]});}
            var Q8;
            Q8=makeQuery(id+"F0.imprint","IMPRINT",FACE,{"disambiguationData":[TD([[makeQuery(id+"F0.imprint","IMPRINT",EDGE,{"derivedFrom":sQuery(id+"F0.wireOp",EDGE,"E4")}),-1.0]])]});
            var Q9;
            Q9=makeQuery(id+"F0.imprint","IMPRINT",FACE,{"disambiguationData":[TD([[makeQuery(id+"F0.imprint","IMPRINT",EDGE,{"derivedFrom":sQuery(id+"F0.wireOp",EDGE,"E7")}),-1.0]])]});
            extrude(context, id + "F4", {"entities" : qUnion([Q0, Q1, Q2, Q3, Q4, Q5, Q6, Q7, Q8, Q9]), "depth" : 6.2 * mm, "offsetDistance" : 25 * mm});
        }
        {
            var Q0;
            {var subQ5=sQuery(id+"F0.wireOp",EDGE,"E35");Q0=makeQuery(id+"F0.imprint","IMPRINT",FACE,{"disambiguationData":[TD([[makeQuery(id+"F0.imprint","IMPRINT",EDGE,{"derivedFrom":subQ5}),-1.0]])]});}
            var Q1;
            {var subQ10=sQuery(id+"F0.wireOp",EDGE,"E26");Q1=makeQuery(id+"F0.imprint","IMPRINT",FACE,{"disambiguationData":[TD([[makeQuery(id+"F0.imprint","IMPRINT",EDGE,{"derivedFrom":subQ10}),-1.0]])]});}
            var Q2;
            {var subQ1=sQuery(id+"F0.wireOp",EDGE,"E19");Q2=makeQuery(id+"F0.imprint","IMPRINT",FACE,{"disambiguationData":[TD([[makeQuery(id+"F0.imprint","IMPRINT",EDGE,{"derivedFrom":subQ1}),1.0]])]});}
            var Q3;
            Q3=makeQuery(id+"F0.imprint","IMPRINT",FACE,{"disambiguationData":[TD([[makeQuery(id+"F0.imprint","IMPRINT",EDGE,{"derivedFrom":sQuery(id+"F0.wireOp",EDGE,"E8")}),-1.0]])]});
            var Q4;
            Q4=makeQuery(id+"F0.imprint","IMPRINT",FACE,{"disambiguationData":[TD([[makeQuery(id+"F0.imprint","IMPRINT",EDGE,{"derivedFrom":sQuery(id+"F0.wireOp",EDGE,"E5")}),-1.0]])]});
            var Q5;
            {var subQ6=sQuery(id+"F0.wireOp",EDGE,"E89");Q5=makeQuery(id+"F0.imprint","IMPRINT",FACE,{"disambiguationData":[TD([[makeQuery(id+"F0.imprint","IMPRINT",EDGE,{"derivedFrom":subQ6}),-1.0]])]});}
            var Q6;
            {var subQ6=sQuery(id+"F0.wireOp",EDGE,"E45");var subQ10=sQuery(id+"F0.wireOp",EDGE,"E44");var subQ11=makeQuery(id+"F0.imprint","INTERSECT",VERTEX,{"disambiguationData":[OD(1.0)],"derivedFrom":[subQ10,subQ6]});Q6=makeQuery(id+"F0.imprint","IMPRINT",FACE,{"disambiguationData":[TD([[makeQuery(id+"F0.imprint","IMPRINT",EDGE,{"disambiguationData":[TD([[subQ11,1.0]])],"derivedFrom":subQ10}),1.0]])]});}
            var Q7;
            {var subQ2=sQuery(id+"F0.wireOp",EDGE,"E81");Q7=makeQuery(id+"F0.imprint","IMPRINT",FACE,{"disambiguationData":[TD([[makeQuery(id+"F0.imprint","IMPRINT",EDGE,{"derivedFrom":subQ2}),-1.0]])]});}
            var Q8;
            {var subQ0=sQuery(id+"F0.wireOp",EDGE,"E51");Q8=makeQuery(id+"F0.imprint","IMPRINT",FACE,{"disambiguationData":[TD([[makeQuery(id+"F0.imprint","IMPRINT",EDGE,{"derivedFrom":subQ0}),1.0]])]});}
            var Q9;
            Q9=makeQuery(id+"F0.imprint","IMPRINT",FACE,{"disambiguationData":[TD([[makeQuery(id+"F0.imprint","IMPRINT",EDGE,{"derivedFrom":sQuery(id+"F0.wireOp",EDGE,"E58")}),-1.0]])]});
            var Q10;
            Q10=makeQuery(id+"F0.imprint","IMPRINT",FACE,{"disambiguationData":[TD([[makeQuery(id+"F0.imprint","IMPRINT",EDGE,{"derivedFrom":sQuery(id+"F0.wireOp",EDGE,"E59")}),-1.0]])]});
            extrude(context, id + "F5", {"entities" : qUnion([Q0, Q1, Q2, Q3, Q4, Q5, Q6, Q7, Q8, Q9, Q10]), "depth" : 6 * mm, "offsetDistance" : 25 * mm});
        }
        {
            var Q0;
            {var subQ2=sQuery(id+"F0.wireOp",EDGE,"E83");Q0=makeQuery(id+"F0.imprint","IMPRINT",FACE,{"disambiguationData":[TD([[makeQuery(id+"F0.imprint","IMPRINT",EDGE,{"derivedFrom":subQ2}),-1.0]])]});}
            var Q1;
            {var subQ4=sQuery(id+"F0.wireOp",EDGE,"E48");Q1=makeQuery(id+"F0.imprint","IMPRINT",FACE,{"disambiguationData":[TD([[makeQuery(id+"F0.imprint","IMPRINT",EDGE,{"derivedFrom":subQ4}),1.0]])]});}
            var Q2;
            {var subQ6=sQuery(id+"F0.wireOp",EDGE,"E90");Q2=makeQuery(id+"F0.imprint","IMPRINT",FACE,{"disambiguationData":[TD([[makeQuery(id+"F0.imprint","IMPRINT",EDGE,{"derivedFrom":subQ6}),1.0]])]});}
            var Q3;
            Q3=makeQuery(id+"F0.imprint","IMPRINT",FACE,{"disambiguationData":[TD([[makeQuery(id+"F0.imprint","IMPRINT",EDGE,{"derivedFrom":sQuery(id+"F0.wireOp",EDGE,"E58")}),1.0]])]});
            var Q4;
            Q4=makeQuery(id+"F0.imprint","IMPRINT",FACE,{"disambiguationData":[TD([[makeQuery(id+"F0.imprint","IMPRINT",EDGE,{"derivedFrom":sQuery(id+"F0.wireOp",EDGE,"E59")}),1.0]])]});
            var Q5;
            {var subQ4=sQuery(id+"F0.wireOp",EDGE,"E64");Q5=makeQuery(id+"F0.imprint","IMPRINT",FACE,{"disambiguationData":[TD([[makeQuery(id+"F0.imprint","IMPRINT",EDGE,{"derivedFrom":subQ4}),1.0]])]});}
            var Q6;
            {var subQ5=sQuery(id+"F0.wireOp",EDGE,"E66");Q6=makeQuery(id+"F0.imprint","IMPRINT",FACE,{"disambiguationData":[TD([[makeQuery(id+"F0.imprint","IMPRINT",EDGE,{"derivedFrom":subQ5}),1.0]])]});}
            extrude(context, id + "F6", {"entities" : qUnion([Q0, Q1, Q2, Q3, Q4, Q5, Q6]), "depth" : 6 * mm, "offsetDistance" : 25 * mm});
        }
        {
            var Q0;
            {var subQ7=sQuery(id+"F0.wireOp",EDGE,"E26");Q0=makeQuery(id+"F0.imprint","IMPRINT",FACE,{"disambiguationData":[TD([[makeQuery(id+"F0.imprint","IMPRINT",EDGE,{"derivedFrom":subQ7}),1.0]])]});}
            var Q1;
            {var subQ0=sQuery(id+"F0.wireOp",EDGE,"E87");Q1=makeQuery(id+"F0.imprint","IMPRINT",FACE,{"disambiguationData":[TD([[makeQuery(id+"F0.imprint","IMPRINT",EDGE,{"derivedFrom":subQ0}),1.0]])]});}
            var Q2;
            {var subQ0=sQuery(id+"F0.wireOp",EDGE,"E54");var subQ1=sQuery(id+"F0.wireOp",EDGE,"E53");var subQ2=makeQuery(id+"F0.imprint","INTERSECT",VERTEX,{"disambiguationData":[OD(0.0)],"derivedFrom":[subQ1,subQ0]});Q2=makeQuery(id+"F0.imprint","IMPRINT",FACE,{"disambiguationData":[TD([[makeQuery(id+"F0.imprint","IMPRINT",EDGE,{"disambiguationData":[TD([[subQ2,1.0]])],"derivedFrom":subQ1}),1.0]])]});}
            var Q3;
            {var subQ5=sQuery(id+"F0.wireOp",EDGE,"E62");Q3=makeQuery(id+"F0.imprint","IMPRINT",FACE,{"disambiguationData":[TD([[makeQuery(id+"F0.imprint","IMPRINT",EDGE,{"derivedFrom":subQ5}),-1.0]])]});}
            var Q4;
            {var subQ3=sQuery(id+"F0.wireOp",EDGE,"E86");Q4=makeQuery(id+"F0.imprint","IMPRINT",FACE,{"disambiguationData":[TD([[makeQuery(id+"F0.imprint","IMPRINT",EDGE,{"derivedFrom":subQ3}),1.0]])]});}
            extrude(context, id + "F7", {"entities" : qUnion([Q0, Q1, Q2, Q3, Q4]), "depth" : 5.8 * mm, "offsetDistance" : 25 * mm});
        }
        {
            var Q0;
            {var subQ3=sQuery(id+"F0.wireOp",EDGE,"E91");Q0=makeQuery(id+"F0.imprint","IMPRINT",FACE,{"disambiguationData":[TD([[makeQuery(id+"F0.imprint","IMPRINT",EDGE,{"derivedFrom":subQ3}),1.0]])]});}
            var Q1;
            {var subQ3=sQuery(id+"F0.wireOp",EDGE,"E67");Q1=makeQuery(id+"F0.imprint","IMPRINT",FACE,{"disambiguationData":[TD([[makeQuery(id+"F0.imprint","IMPRINT",EDGE,{"derivedFrom":subQ3}),-1.0]])]});}
            var Q2;
            {var subQ3=sQuery(id+"F0.wireOp",EDGE,"E84");Q2=makeQuery(id+"F0.imprint","IMPRINT",FACE,{"disambiguationData":[TD([[makeQuery(id+"F0.imprint","IMPRINT",EDGE,{"derivedFrom":subQ3}),-1.0]])]});}
            var Q3;
            {var subQ0=sQuery(id+"F0.wireOp",EDGE,"E85");Q3=makeQuery(id+"F0.imprint","IMPRINT",FACE,{"disambiguationData":[TD([[makeQuery(id+"F0.imprint","IMPRINT",EDGE,{"derivedFrom":subQ0}),1.0]])]});}
            extrude(context, id + "F8", {"entities" : qUnion([Q0, Q1, Q2, Q3]), "depth" : 5.6 * mm, "offsetDistance" : 25 * mm});
        }
        {
            var Q0;
            {var subQ0=sQuery(id+"F0.wireOp",EDGE,"E82");var subQ1=sQuery(id+"F0.wireOp",EDGE,"E70");var subQ2=makeQuery(id+"F0.imprint","INTERSECT",VERTEX,{"derivedFrom":[subQ1,subQ0]});Q0=makeQuery(id+"F0.imprint","IMPRINT",FACE,{"disambiguationData":[TD([[makeQuery(id+"F0.imprint","IMPRINT",EDGE,{"disambiguationData":[TD([[subQ2,1.0]])],"derivedFrom":subQ1}),-1.0]])]});}
            var Q1;
            {var subQ2=sQuery(id+"F0.wireOp",EDGE,"E56");Q1=makeQuery(id+"F0.imprint","IMPRINT",FACE,{"disambiguationData":[TD([[makeQuery(id+"F0.imprint","IMPRINT",EDGE,{"derivedFrom":subQ2}),-1.0]])]});}
            var Q2;
            {var subQ0=sQuery(id+"F0.wireOp",EDGE,"E83");var subQ1=sQuery(id+"F0.wireOp",EDGE,"E82");var subQ2=makeQuery(id+"F0.imprint","INTERSECT",VERTEX,{"disambiguationData":[OD(1.0)],"derivedFrom":[subQ1,subQ0]});Q2=makeQuery(id+"F0.imprint","IMPRINT",FACE,{"disambiguationData":[TD([[makeQuery(id+"F0.imprint","IMPRINT",EDGE,{"disambiguationData":[TD([[subQ2,-1.0]])],"derivedFrom":subQ1}),-1.0]])]});}
            extrude(context, id + "F9", {"entities" : qUnion([Q0, Q1, Q2]), "depth" : 5.6 * mm, "offsetDistance" : 25 * mm});
        }
        {
            var Q0;
            {var subQ3=sQuery(id+"F0.wireOp",EDGE,"E64");Q0=makeQuery(id+"F0.imprint","IMPRINT",FACE,{"disambiguationData":[TD([[makeQuery(id+"F0.imprint","IMPRINT",EDGE,{"derivedFrom":subQ3}),-1.0]])]});}
            extrude(context, id + "F10", {"entities" : qUnion([Q0]), "depth" : 5.4 * mm, "offsetDistance" : 25 * mm});
        }
        {
            var Q0;
            Q0=qCreatedBy(makeId("Top.planeOp"),FACE);
            var sketch = newSketch(context, id + "F11", { "sketchPlane" : qUnion([Q0])});
            skLineSegment(sketch, "E92.bottom", {"start": v(-9.97, 21.54) * mm, "end": v(9.03, 21.54) * mm});
            skLineSegment(sketch, "E92.top", {"start": v(-9.97, -21.46) * mm, "end": v(9.03, -21.46) * mm});
            skLineSegment(sketch, "E92.left", {"start": v(-14.97, 16.54) * mm, "end": v(-14.97, -16.46) * mm});
            skLineSegment(sketch, "E92.right", {"start": v(14.03, 16.54) * mm, "end": v(14.03, -16.46) * mm});
            skLineSegment(sketch, "E93.bottom", {"start": v(-9.97, 23.54) * mm, "end": v(9.03, 23.54) * mm});
            skLineSegment(sketch, "E93.top", {"start": v(-15.97, -31.46) * mm, "end": v(9.03, -31.46) * mm});
            skLineSegment(sketch, "E93.left", {"start": v(-16.97, 16.54) * mm, "end": v(-16.97, -30.46) * mm});
            skLineSegment(sketch, "E93.right", {"start": v(16.03, 16.54) * mm, "end": v(16.03, -24.46) * mm});
            skPoint(sketch, "E94.visualSharp", {"position": v(-14.97, 21.54) * mm});
            skArc(sketch, "E94.filletArc", {"start": v(-9.97, 21.54) * mm, "mid": v(-13.5, 20.07) * mm, "end": v(-14.97, 16.54) * mm});
            skPoint(sketch, "E95.visualSharp", {"position": v(14.03, 21.54) * mm});
            skArc(sketch, "E95.filletArc", {"start": v(14.03, 16.54) * mm, "mid": v(12.56, 20.07) * mm, "end": v(9.03, 21.54) * mm});
            skPoint(sketch, "E96.visualSharp", {"position": v(14.03, -21.46) * mm});
            skArc(sketch, "E96.filletArc", {"start": v(9.03, -21.46) * mm, "mid": v(12.56, -20) * mm, "end": v(14.03, -16.46) * mm});
            skPoint(sketch, "E97.visualSharp", {"position": v(16.03, 23.54) * mm});
            skArc(sketch, "E97.filletArc", {"start": v(16.03, 16.54) * mm, "mid": v(13.98, 21.49) * mm, "end": v(9.03, 23.54) * mm});
            skPoint(sketch, "E98.visualSharp", {"position": v(16.03, -31.46) * mm});
            skArc(sketch, "E98.filletArc", {"start": v(9.03, -31.46) * mm, "mid": v(13.98, -29.41) * mm, "end": v(16.03, -24.46) * mm});
            skPoint(sketch, "E99.visualSharp", {"position": v(-16.97, 23.54) * mm});
            skArc(sketch, "E99.filletArc", {"start": v(-9.97, 23.54) * mm, "mid": v(-14.92, 21.49) * mm, "end": v(-16.97, 16.54) * mm});
            skPoint(sketch, "E100.visualSharp", {"position": v(-14.97, -21.46) * mm});
            skArc(sketch, "E100.filletArc", {"start": v(-14.97, -16.46) * mm, "mid": v(-13.5, -20) * mm, "end": v(-9.97, -21.46) * mm});
            skPoint(sketch, "E101.visualSharp", {"position": v(-16.97, -31.46) * mm});
            skArc(sketch, "E101.filletArc", {"start": v(-16.97, -30.46) * mm, "mid": v(-16.68, -31.17) * mm, "end": v(-15.97, -31.46) * mm});
            skCircle(sketch, "E102", {"center": v(0, 33.54) * mm, "radius": 6 * mm});
            skCircle(sketch, "E103", {"center": v(0, 33.54) * mm, "radius": 4 * mm});
            skArc(sketch, "E104", {"start": v(-8.98, 23.54) * mm, "mid": v(-5.3, 26.22) * mm, "end": v(-5.32, 30.77) * mm});
            skLineSegment(sketch, "E105.bottom", {"start": v(-3.1, 27.24) * mm, "end": v(3.1, 27.24) * mm});
            skLineSegment(sketch, "E105.top", {"start": v(-4.1, 23.54) * mm, "end": v(4.1, 23.54) * mm});
            skLineSegment(sketch, "E105.left", {"start": v(-4.1, 26.24) * mm, "end": v(-4.1, 23.54) * mm});
            skLineSegment(sketch, "E105.right", {"start": v(4.1, 26.24) * mm, "end": v(4.1, 23.54) * mm});
            skPoint(sketch, "E106.visualSharp", {"position": v(-4.1, 27.24) * mm});
            skArc(sketch, "E106.filletArc", {"start": v(-3.1, 27.24) * mm, "mid": v(-3.8, 26.95) * mm, "end": v(-4.1, 26.24) * mm});
            skPoint(sketch, "E107.visualSharp", {"position": v(4.1, 27.24) * mm});
            skArc(sketch, "E107.filletArc", {"start": v(4.1, 26.24) * mm, "mid": v(3.8, 26.95) * mm, "end": v(3.1, 27.24) * mm});
            skArc(sketch, "E108", {"start": v(5.41, 30.95) * mm, "mid": v(5.75, 26.53) * mm, "end": v(9.03, 23.54) * mm});
            skSolve(sketch);
        }
        {
            var Q0;
            Q0=makeQuery(id+"F11.imprint","IMPRINT",FACE,{"disambiguationData":[TD([[makeQuery(id+"F11.imprint","IMPRINT",EDGE,{"derivedFrom":sQuery(id+"F11.wireOp",EDGE,"E92.bottom")}),1.0]])]});
            extrude(context, id + "F12", {"entities" : qUnion([Q0]), "depth" : 6 * mm, "offsetDistance" : 25 * mm});
        }
        {
            var Q0;
            Q0=makeQuery(id+"F12.opExtrude","CAP_EDGE",EDGE,{"disambiguationData":[OSD([sQuery(id+"F11.wireOp",EDGE,"E98.filletArc")])],"isStart":false});
            fillet(context, id + "F13", {"entities" : qUnion([Q0]), "radius" : 1.5 * mm, "tangentPropagation" : true, "allowEdgeOverflow" : false});
        }
        {
            var Q0;
            Q0=makeQuery(id+"F11.imprint","IMPRINT",FACE,{"disambiguationData":[TD([[makeQuery(id+"F11.imprint","IMPRINT",EDGE,{"derivedFrom":sQuery(id+"F11.wireOp",EDGE,"E103")}),-1.0]])]});
            extrude(context, id + "F14", {"entities" : qUnion([Q0]), "depth" : 6 * mm, "offsetDistance" : 25 * mm});
        }
        {
            var Q0;
            {var subQ0=sQuery(id+"F11.wireOp",EDGE,"E104");Q0=makeQuery(id+"F11.imprint","IMPRINT",FACE,{"disambiguationData":[TD([[makeQuery(id+"F11.imprint","IMPRINT",EDGE,{"derivedFrom":subQ0}),-1.0]])]});}
            extrude(context, id + "F15", {"entities" : qUnion([Q0]), "depth" : 4.4 * mm, "offsetDistance" : 25 * mm});
        }
        {
            var Q0;
            Q0=makeQuery(id+"F14.opExtrude","CAP_FACE",FACE,{"disambiguationData":[OSD([sQuery(id+"F11.wireOp",EDGE,"E102"),sQuery(id+"F11.wireOp",EDGE,"E103")])],"isStart":false});
            fillet(context, id + "F16", {"entities" : qUnion([Q0]), "radius" : 1 * mm, "tangentPropagation" : true, "allowEdgeOverflow" : false});
        }
        {
            var Q0;
            Q0=makeQuery(id+"F15.opExtrude","CAP_EDGE",EDGE,{"disambiguationData":[OSD([sQuery(id+"F11.wireOp",EDGE,"aUvm8erm-xxqf-If5a-6mQM-qNdrGN8eYJHd")])],"isStart":false});
            var Q1;
            Q1=makeQuery(id+"F15.opExtrude","CAP_EDGE",EDGE,{"disambiguationData":[OSD([sQuery(id+"F11.wireOp",EDGE,"E104")])],"isStart":false});
            var Q2;
            Q2=makeQuery(id+"F15.opExtrude","CAP_EDGE",EDGE,{"disambiguationData":[OSD([sQuery(id+"F11.wireOp",EDGE,"E108")])],"isStart":false});
            fillet(context, id + "F17", {"entities" : qUnion([Q0, Q1, Q2]), "radius" : 1 * mm, "tangentPropagation" : true, "allowEdgeOverflow" : false});
        }
        {
            var Q0;
            Q0=makeQuery(id+"F12.opExtrude","SWEPT_FACE",FACE,{"disambiguationData":[OSD([sQuery(id+"F11.wireOp",EDGE,"E92.bottom")])]});
            var sketch = newSketch(context, id + "F18", { "sketchPlane" : qUnion([Q0])});
            skCircle(sketch, "E109", {"center": v(0, 2.8) * mm, "radius": 1.5 * mm});
            skSolve(sketch);
        }
        {
            var Q0;
            Q0=makeQuery(id+"F18.imprint","IMPRINT",FACE,{"disambiguationData":[TD([[makeQuery(id+"F18.imprint","IMPRINT",EDGE,{"derivedFrom":sQuery(id+"F18.wireOp",EDGE,"E109")}),-1.0]])]});
            var sketch = newSketch(context, id + "F19", { "sketchPlane" : qUnion([Q0])});
            skCircle(sketch, "E110", {"center": v(0, 2.8) * mm, "radius": 1.8 * mm});
            skSolve(sketch);
        }
        {
            var Q0;
            Q0 = qSketchRegion(id + "F19", true);
            extrude(context, id + "F20", {"entities" : qUnion([Q0]), "operationType" : NewBodyOperationType.REMOVE, "oppositeDirection" : true, "depth" : 3 * mm, "offsetDistance" : 25 * mm});
        }
        {
            var Q0;
            Q0=makeQuery(id+"F18.imprint","IMPRINT",FACE,{"disambiguationData":[TD([[makeQuery(id+"F18.imprint","IMPRINT",EDGE,{"derivedFrom":sQuery(id+"F18.wireOp",EDGE,"E109")}),1.0]])]});
            var Q1;
            Q1=sQuery(id+"F18.wireOp",EDGE,"E109");
            extrude(context, id + "F21", {"entities" : qUnion([Q0]), "surfaceEntities" : qUnion([Q1]), "depth" : 7 * mm, "offsetDistance" : 25 * mm, "hasSecondDirection" : true, "secondDirectionOppositeDirection" : true, "secondDirectionDepth" : 4 * mm});
        }
        {
            var Q0;
            Q0=qCreatedBy(makeId("Top.planeOp"),FACE);
            var sketch = newSketch(context, id + "F22", { "sketchPlane" : qUnion([Q0])});
            skLineSegment(sketch, "E111.bottom", {"start": v(2.4, 24.17) * mm, "end": v(-2.4, 24.17) * mm});
            skLineSegment(sketch, "E111.top", {"start": v(2.4, 26.47) * mm, "end": v(-2.4, 26.47) * mm});
            skLineSegment(sketch, "E111.left", {"start": v(2.4, 24.17) * mm, "end": v(2.4, 26.47) * mm});
            skLineSegment(sketch, "E111.right", {"start": v(-2.4, 24.17) * mm, "end": v(-2.4, 26.47) * mm});
            skPoint(sketch, "E111.middle", {"position": v(0, 25.32) * mm});
            skSolve(sketch);
        }
        {
            var Q0;
            Q0=makeQuery(id+"F22.imprint","IMPRINT",FACE,{"disambiguationData":[TD([[makeQuery(id+"F22.imprint","IMPRINT",EDGE,{"derivedFrom":sQuery(id+"F22.wireOp",EDGE,"E111.bottom")}),-1.0]])]});
            extrude(context, id + "F23", {"entities" : qUnion([Q0]), "operationType" : NewBodyOperationType.ADD, "depth" : 5 * mm, "offsetDistance" : 25 * mm});
        }
        {
            var Q0;
            Q0=makeQuery(id+"F23.opExtrude","CAP_EDGE",EDGE,{"disambiguationData":[OSD([sQuery(id+"F22.wireOp",EDGE,"E111.right")])],"isStart":false});
            var Q1;
            Q1=makeQuery(id+"F23.opExtrude","CAP_EDGE",EDGE,{"disambiguationData":[OSD([sQuery(id+"F22.wireOp",EDGE,"E111.left")])],"isStart":false});
            var Q2;
            Q2=makeQuery(id+"F23.opExtrude","CAP_EDGE",EDGE,{"disambiguationData":[OSD([sQuery(id+"F22.wireOp",EDGE,"E111.right")])],"isStart":true});
            var Q3;
            Q3=makeQuery(id+"F23.opExtrude","CAP_EDGE",EDGE,{"disambiguationData":[OSD([sQuery(id+"F22.wireOp",EDGE,"E111.left")])],"isStart":true});
            fillet(context, id + "F24", {"entities" : qUnion([Q0, Q1, Q2, Q3]), "radius" : 1 * mm, "tangentPropagation" : true, "allowEdgeOverflow" : false});
        }
    });
